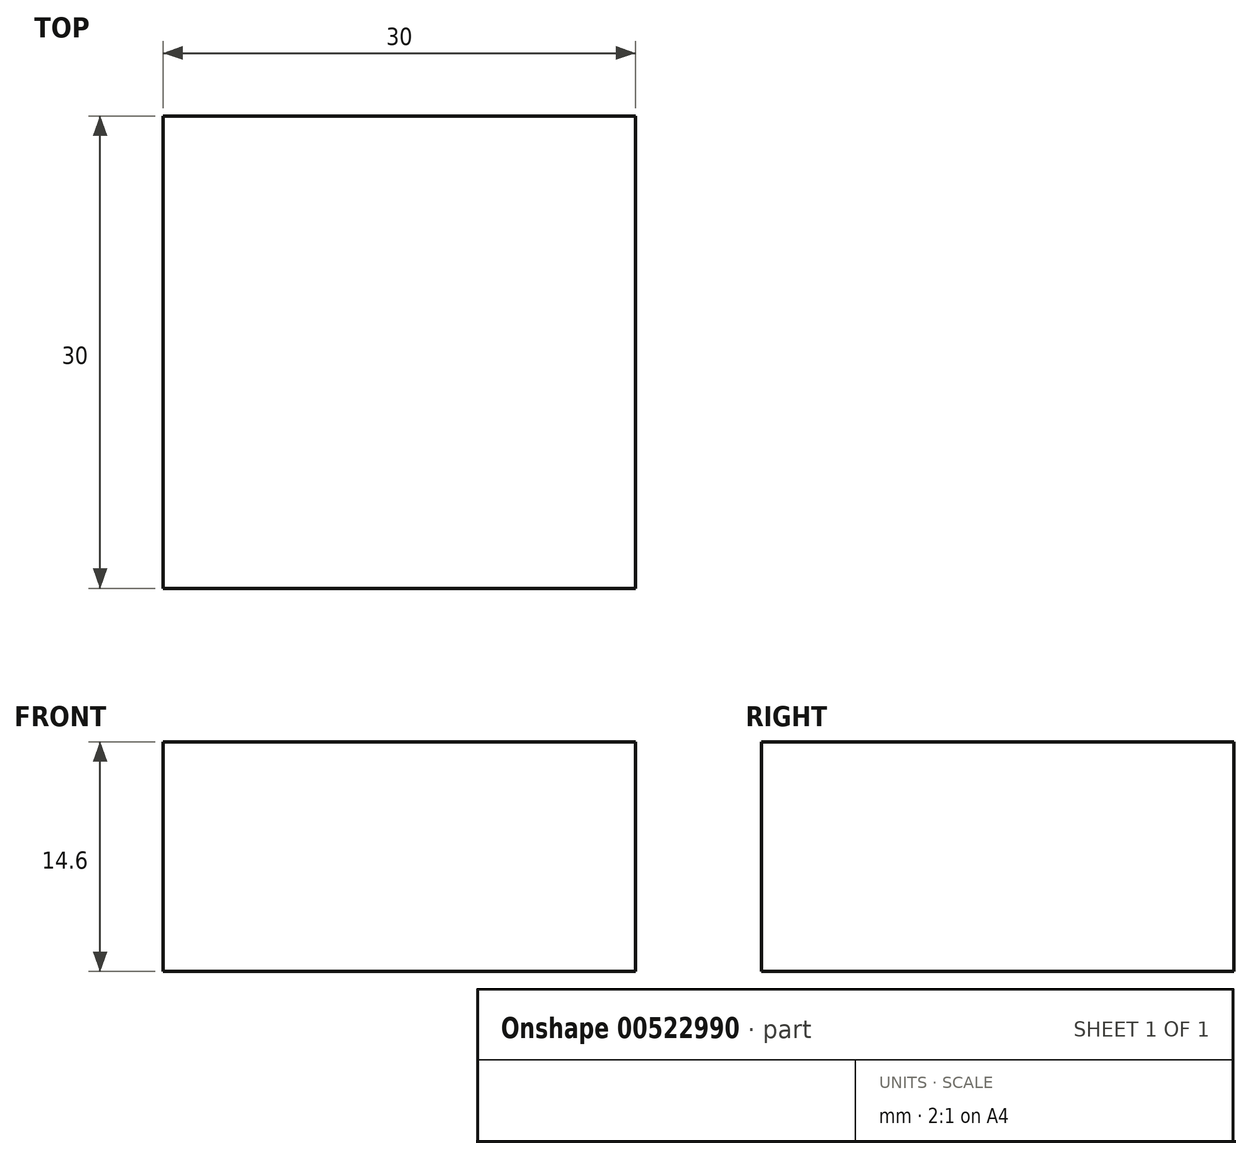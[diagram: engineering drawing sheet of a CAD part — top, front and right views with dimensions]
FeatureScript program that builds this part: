
annotation { "Feature Type Name" : "Feature", "Feature Type Description" : "" }
export const myFeature = defineFeature(function(context is Context, id is Id, definition is map)
    precondition{}
    {
        {
            var Q0;
            Q0=qCreatedBy(makeId("Top.planeOp"),FACE);
            var sketch = newSketch(context, id + "F0", { "sketchPlane" : qUnion([Q0])});
            skLineSegment(sketch, "E0.bottom", {"start": v(0, 0) * mm, "end": v(30, 0) * mm});
            skLineSegment(sketch, "E0.top", {"start": v(0, -30) * mm, "end": v(30, -30) * mm});
            skLineSegment(sketch, "E0.left", {"start": v(0, 0) * mm, "end": v(0, -30) * mm});
            skLineSegment(sketch, "E0.right", {"start": v(30, 0) * mm, "end": v(30, -30) * mm});
            skSolve(sketch);
        }
        {
            var Q0;
            Q0=makeQuery(id+"F0.imprint","IMPRINT",FACE,{"disambiguationData":[TD([[makeQuery(id+"F0.imprint","IMPRINT",EDGE,{"derivedFrom":sQuery(id+"F0.wireOp",EDGE,"E0.bottom")}),-1.0]])]});
            extrude(context, id + "F1", {"entities" : qUnion([Q0]), "depth" : 14.6 * mm, "offsetDistance" : 25 * mm});
        }
    });
